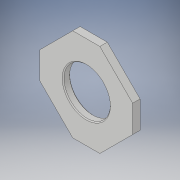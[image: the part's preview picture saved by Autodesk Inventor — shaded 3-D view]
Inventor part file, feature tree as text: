
AUTODESK INVENTOR PART (.ipt)
format: ipt  version: 2019 (Build 230136000, 136)  size: 119,296 bytes
history: native  units: mm
features: extrude x1, chamfer x1, sketch x1
ambient origin geometry x8: Origin, YZ Plane, XZ Plane, XY Plane, X Axis, Y Axis, Z Axis, Center Point
bodies: Solide1 (feature_tree)
feature tree (3):
  extrude  "Extrusion1"  Depth=50.0mm
  chamfer  "Chanfrein1"  Distance=8.0mm
  sketch  "Esquisse1"
